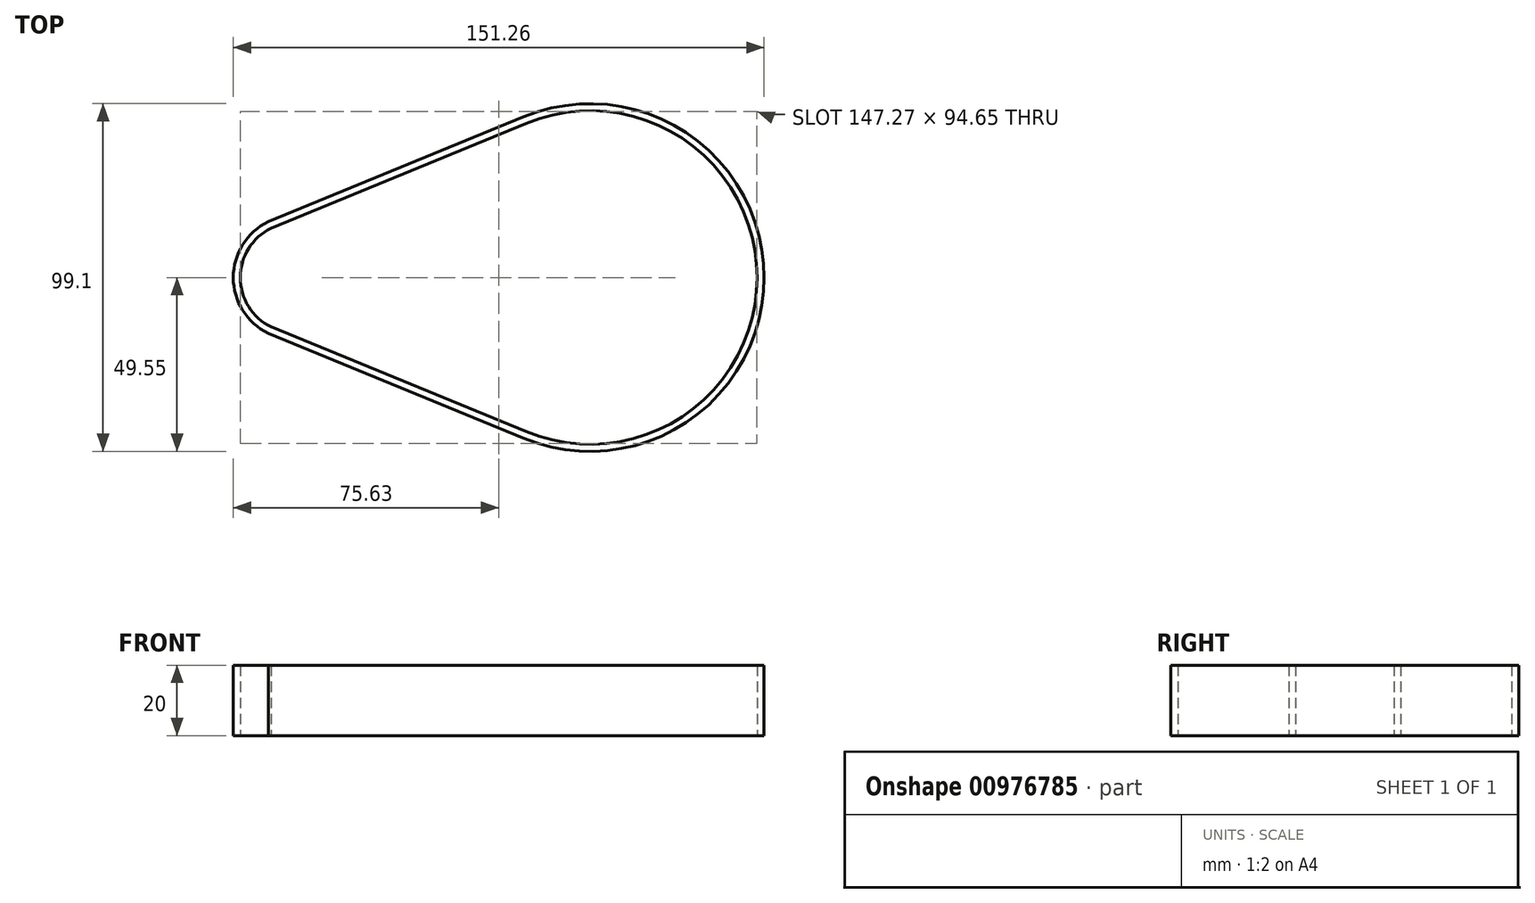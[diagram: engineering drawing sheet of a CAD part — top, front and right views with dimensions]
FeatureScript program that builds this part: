
annotation { "Feature Type Name" : "Feature", "Feature Type Description" : "" }
export const myFeature = defineFeature(function(context is Context, id is Id, definition is map)
    precondition{}
    {
        {
            var Q0;
            Q0=qCreatedBy(makeId("Top.planeOp"),FACE);
            var sketch = newSketch(context, id + "F0", { "sketchPlane" : qUnion([Q0])});
            skArc(sketch, "E0", {"start": v(7.82, -43.9) * mm, "mid": v(73.63, 0) * mm, "end": v(7.82, 43.9) * mm});
            skLineSegment(sketch, "E1", {"start": v(7.82, 43.9) * mm, "end": v(-64.85, 14.07) * mm});
            skArc(sketch, "E2", {"start": v(-64.85, 14.07) * mm, "mid": v(-73.63, 0) * mm, "end": v(-64.85, -14.07) * mm});
            skLineSegment(sketch, "E3", {"start": v(-64.85, -14.07) * mm, "end": v(7.82, -43.9) * mm});
            skArc(sketch, "E4.0", {"start": v(-65.67, 15.9) * mm, "mid": v(-75.63, 0) * mm, "end": v(-65.67, -15.9) * mm});
            skLineSegment(sketch, "E4.1", {"start": v(7.05, 45.74) * mm, "end": v(-65.67, 15.9) * mm});
            skArc(sketch, "E4.2", {"start": v(7.05, -45.74) * mm, "mid": v(75.63, 0) * mm, "end": v(7.05, 45.74) * mm});
            skLineSegment(sketch, "E4.3", {"start": v(-65.67, -15.9) * mm, "end": v(7.05, -45.74) * mm});
            skSolve(sketch);
        }
        {
            var Q0;
            Q0=makeQuery(id+"F0.imprint","IMPRINT",FACE,{"disambiguationData":[TD([[makeQuery(id+"F0.imprint","IMPRINT",EDGE,{"derivedFrom":sQuery(id+"F0.wireOp",EDGE,"E0")}),-1.0]])]});
            extrude(context, id + "F1", {"entities" : qUnion([Q0]), "depth" : 20 * mm, "offsetDistance" : 25 * mm});
        }
    });
